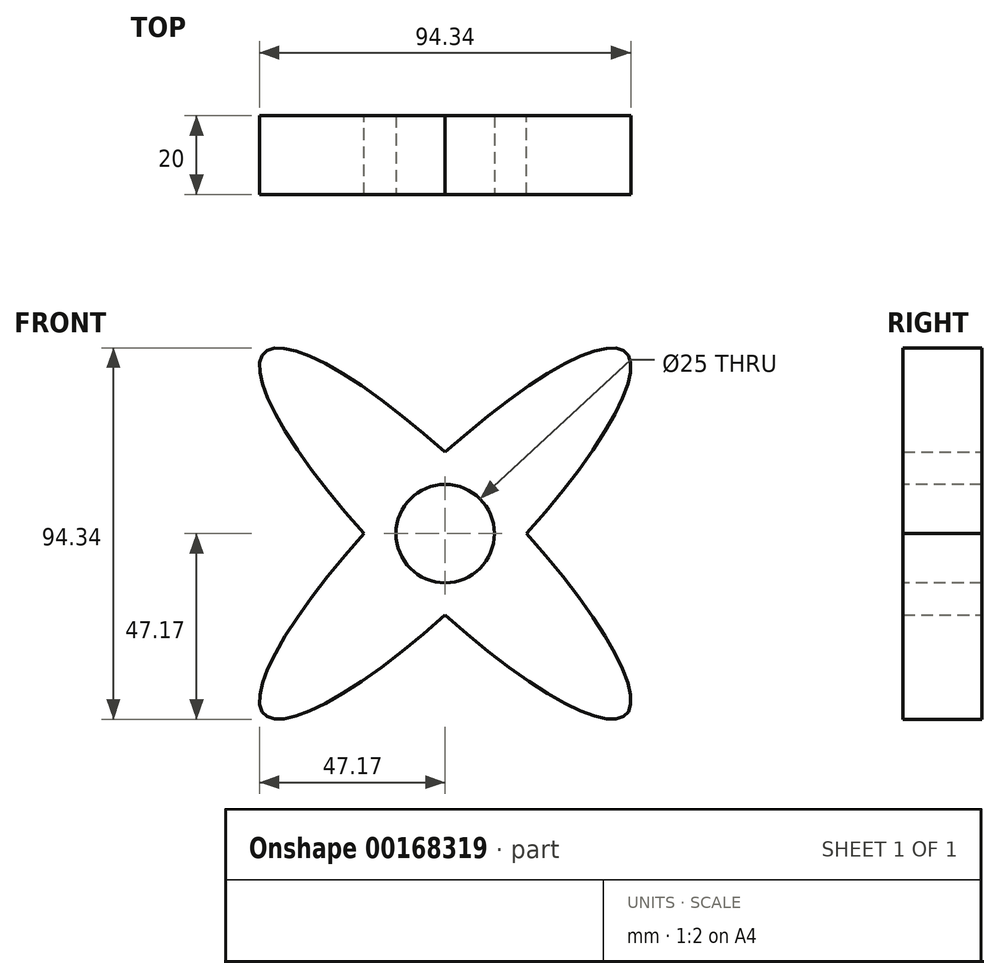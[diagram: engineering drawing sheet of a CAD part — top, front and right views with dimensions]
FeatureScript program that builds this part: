
annotation { "Feature Type Name" : "Feature", "Feature Type Description" : "" }
export const myFeature = defineFeature(function(context is Context, id is Id, definition is map)
    precondition{}
    {
        {
            var Q0;
            Q0=qCreatedBy(makeId("Front.planeOp"),FACE);
            var sketch = newSketch(context, id + "F0", { "sketchPlane" : qUnion([Q0])});
            skEllipse(sketch, "E0", {"center": v(0, 0) * mm, "majorRadius": 65 * mm, "minorRadius": 15 * mm, "majorAxis": v(0.7, 0.7)});
            skEllipse(sketch, "E1", {"center": v(0, 0) * mm, "majorRadius": 65 * mm, "minorRadius": 15 * mm, "majorAxis": v(-0.7, 0.7)});
            skLineSegment(sketch, "E2", {"start": v(45.96, 45.96) * mm, "end": v(0, 0) * mm, "construction": true});
            skLineSegment(sketch, "E3", {"start": v(0, 0) * mm, "end": v(75.13, 0) * mm, "construction": true});
            skLineSegment(sketch, "E4", {"start": v(-45.96, 45.96) * mm, "end": v(0, 0) * mm, "construction": true});
            skLineSegment(sketch, "E5", {"start": v(0, 0) * mm, "end": v(-73.73, 0) * mm, "construction": true});
            skSolve(sketch);
        }
        {
            var Q0;
            Q0 = qSketchRegion(id + "F0", true);
            extrude(context, id + "F1", {"entities" : qUnion([Q0]), "depth" : 20 * mm});
        }
        {
            var Q0;
            Q0=makeQuery(id+"F1.opExtrude","CAP_FACE",FACE,{"disambiguationData":[OSD([sQuery(id+"F0.wireOp",EDGE,"E0"),sQuery(id+"F0.wireOp",EDGE,"E1")])],"isStart":false});
            var sketch = newSketch(context, id + "F2", { "sketchPlane" : qUnion([Q0])});
            skCircle(sketch, "E6", {"center": v(0, 0) * mm, "radius": 12.5 * mm});
            skSolve(sketch);
        }
        {
            var Q0;
            Q0 = qSketchRegion(id + "F2", true);
            extrude(context, id + "F3", {"entities" : qUnion([Q0]), "operationType" : NewBodyOperationType.REMOVE, "oppositeDirection" : true, "depth" : 20 * mm});
        }
    });
